# Revit family: Sink-Top_Mount-Kitchen-KOHLER-Northland-K-6579
name_source: partatom
category: Plumbing Fixtures
units: mm (PartAtom-declared; Revit-internal decimal feet)

## family parameters
Cut with Voids When Loaded = No
Host = Face
Maintain Annotation Orientation = No
OmniClass Number = 23.31.13.00
OmniClass Title = Sinks
Part Type = Normal
Room Calculation Point = No
Round Connector Dimension = Use Diameter
Shared = No

## types (11) — shared parameters
ADA Compliant = No
Assembly Code = D2010400
CW Connection = No
Cold Water Inlet = Cold Water Inlet
Date Modified = 05/30/2025
Default Elevation = 36"
Description = 15 x 15 Inch SR Entertainment Sink
Drain Included = No
HW Connection = No
Height = 10"
Hot Water Inlet = Hot Water Inlet
Length = 15"
Manufacturer = Kohler Co.
Master Format 2014 = 22 41 16
Master Format 2014 Name = Residential Lavatories and Sinks
Material = Enameled Cast Iron
Product Documentation Link = https://www.us.kohler.com
Product Name = Northland
Product Page URL = http://www.us.kohler.com
URL = https://www.us.kohler.com
Vent Connection = No
Waste Connection = Yes
Waste Water Outlet = Waste Water Outlet
WaterSense Certified = No
Width = 15"

## per-type parameters (varying)
| type | Finish | Model | One Hole Faucet | Two Hole Faucet | Type |
| Two Hole, 0-White | KOHLER-Enameled_Cast_Iron-0-White | K-6579-2-0 | No | Yes | 4 |
| Two Hole, 97-Timberline | KOHLER-Enameled_Cast_Iron-97-Timberline | K-6579-2-97 | No | Yes | 9 |
| One Hole, 0-White | KOHLER-Enameled_Cast_Iron-0-White | K-6579-1-0 | Yes | No | 1 |
| One Hole, 7-Black Black | KOHLER-Enameled_Cast_Iron-7-Black_Black | K-6579-1-7 | Yes | No | 2 |
| Two Hole, 7-Black Black | KOHLER-Enameled_Cast_Iron-7-Black_Black | K-6579-2-7 | No | Yes | 6 |
| One Hole, 96-Biscuit | KOHLER-Enameled_Cast_Iron-96-Biscuit | K-6579-1-96 | Yes | No | 3 |
| Two Hole, 33-Mexican Sand | KOHLER-Enameled_Cast_Iron-33-Mexican_Sand | K-6579-2-33 | No | Yes | 5 |
| Two Hole, 95-Ice Grey | KOHLER-Enameled_Cast_Iron-95-Ice_Grey | K-6579-2-95 | No | Yes | 7 |
| Two Hole, 96-Buscuit | KOHLER-Enameled_Cast_Iron-96-Biscuit | K-6579-2-96 | No | Yes | 8 |
| Two Hole, G9-Sandbar | KOHLER-Enameled_Cast_Iron-G9-Sandbar | K-6579-2-G9 | No | Yes | 10 |
| Two Hole, K4-Cashmere | KOHLER-Enameled_Cast_Iron-K4-Cashmere | K-6579-2-K4 | No | Yes | 11 |

## geometry (parser evidence)
native form markers: Sweep x5
no freeform markers — native parametric forms only
